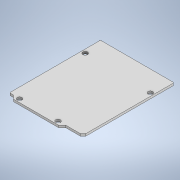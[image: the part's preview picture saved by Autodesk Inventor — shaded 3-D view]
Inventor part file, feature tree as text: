
AUTODESK INVENTOR PART (.ipt)
format: ipt  version: 2021 (Build 250183000, 183)  size: 133,120 bytes
history: native  units: mm
features: chamfer x2, sketch x2, extrude x1, hole x1
ambient origin geometry x8: Origin, YZ Plane, XZ Plane, XY Plane, X Axis, Y Axis, Z Axis, Center Point
bodies: Solid1 (feature_tree)
feature tree (6):
  extrude  "Extrusion1"  Depth=68.75mm
  chamfer  "Chamfer1"  Distance=2.85mm
  chamfer  "Chamfer2"  Distance=2.56mm
  hole  "Hole1"  [1 undecoded]
  sketch  "Sketch1"  dims[d2=53.5mm d12=68.75mm]
  sketch  "Sketch2"  dims[d13=2.6mm d14=2.85mm d15=2.56mm d16=32.86mm d17=12.6mm d18=28.0mm d19=26.0mm d20=1.6mm d21=0.0mm d22=2.0mm d23=2.0mm d24=45.0deg d25=0.5mm d26=2.0mm d27=45.0deg d28=2.7mm d29=13.79mm d30=2.18mm d31=15.0mm d32=7.48mm d33=2.38mm d34=18.0mm d35=3.4mm d36=6.0mm d37=6.3mm d38=2.0mm d39=90.0deg d40=8.0mm d41=20.594885mm]
note: 1 required parameter value undecoded (feature->parameter linkage not recoverable at this tier; creation-order binding heuristic only, values carry confidence <= 0.55)
